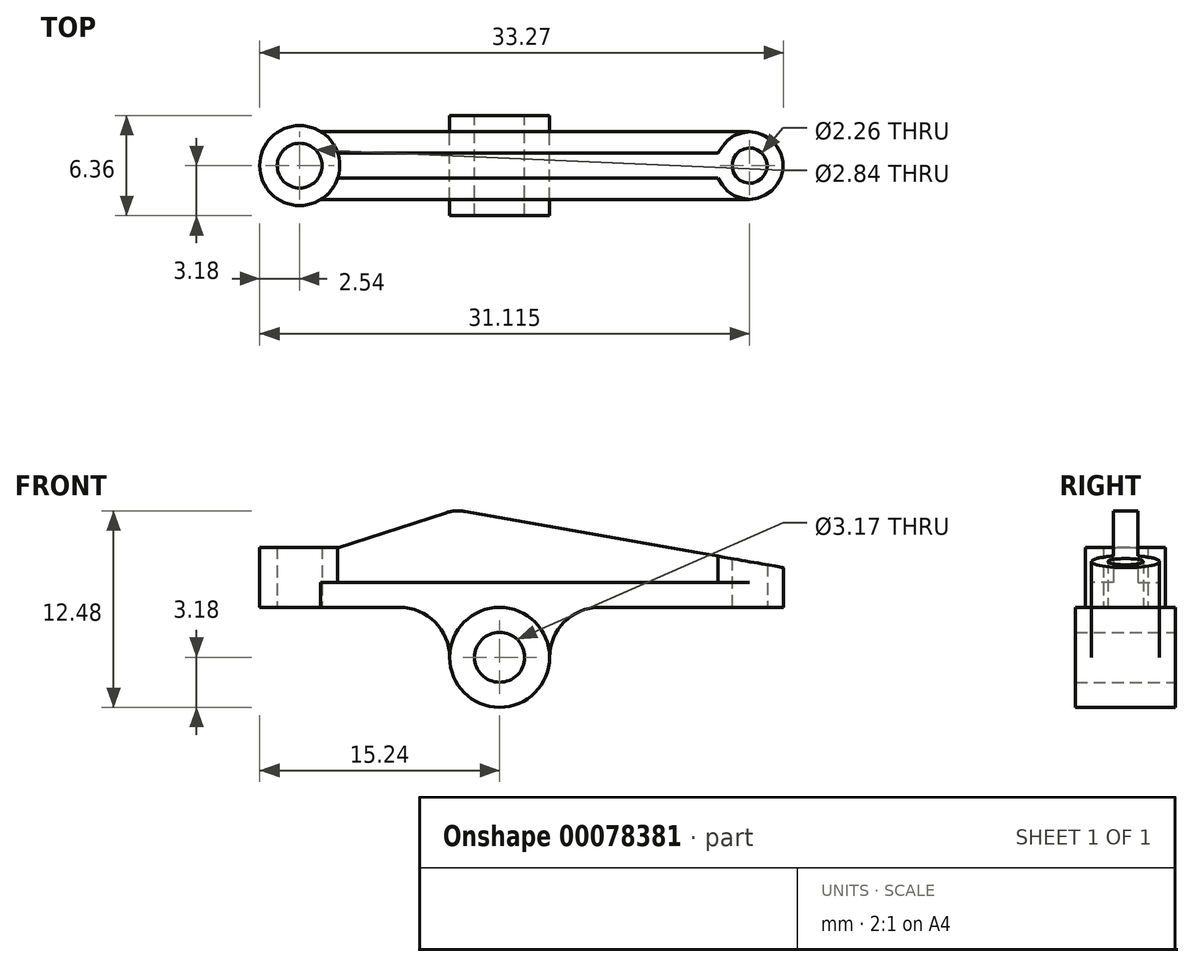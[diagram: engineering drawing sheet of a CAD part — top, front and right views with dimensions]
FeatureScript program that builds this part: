
annotation { "Feature Type Name" : "Feature", "Feature Type Description" : "" }
export const myFeature = defineFeature(function(context is Context, id is Id, definition is map)
    precondition{}
    {
        {
            var Q0;
            Q0=qCreatedBy(makeId("Front.planeOp"),FACE);
            var sketch = newSketch(context, id + "F0", { "sketchPlane" : qUnion([Q0])});
            skCircle(sketch, "E0", {"center": v(0, 0) * mm, "radius": 1.59 * mm});
            skCircle(sketch, "E1", {"center": v(0, 0) * mm, "radius": 3.18 * mm});
            skSolve(sketch);
        }
        {
            var Q0;
            Q0 = qSketchRegion(id + "F0", true);
            extrude(context, id + "F1", {"entities" : qUnion([Q0]), "endBound" : BoundingType.SYMMETRIC, "depth" : 6.35 * mm});
        }
        {
            var Q0;
            Q0=qCreatedBy(makeId("Front.planeOp"),FACE);
            var sketch = newSketch(context, id + "F2", { "sketchPlane" : qUnion([Q0])});
            skLineSegment(sketch, "E2", {"start": v(0, 0) * mm, "end": v(0, 3.18) * mm, "construction": true});
            skSolve(sketch);
        }
        {
            var Q0;
            Q0=qCreatedBy(makeId("Top.planeOp"),FACE);
            cPlane(context, id + "F3", {"entities" : qUnion([Q0]), "cplaneType" : CPlaneType.OFFSET, "offset" : 3.17 * mm, "width" : 152.4 * mm, "height" : 152.4 * mm});
        }
        {
            var Q0;
            Q0=qCreatedBy(id+"F3.planeOp",FACE);
            var sketch = newSketch(context, id + "F4", { "sketchPlane" : qUnion([Q0])});
            skCircle(sketch, "E3", {"center": v(-12.7, 0) * mm, "radius": 1.42 * mm});
            skCircle(sketch, "E4", {"center": v(15.88, 0) * mm, "radius": 1.13 * mm});
            skCircle(sketch, "E5", {"center": v(-12.7, 0) * mm, "radius": 2.54 * mm});
            skCircle(sketch, "E6", {"center": v(15.88, 0) * mm, "radius": 2.16 * mm});
            skSolve(sketch);
        }
        {
            var Q0;
            Q0=qCreatedBy(makeId("Front.planeOp"),FACE);
            var sketch = newSketch(context, id + "F5", { "sketchPlane" : qUnion([Q0])});
            skLineSegment(sketch, "E7", {"start": v(-10.16, 6.99) * mm, "end": v(-3.41, 9.18) * mm});
            skLineSegment(sketch, "E8", {"start": v(-2.19, 9.26) * mm, "end": v(14.01, 6.4) * mm});
            skLineSegment(sketch, "E9", {"start": v(14.01, 6.4) * mm, "end": v(14.01, 3.19) * mm});
            skLineSegment(sketch, "E10", {"start": v(-10.16, 3.18) * mm, "end": v(14.01, 3.19) * mm});
            skPoint(sketch, "E11.visualSharp", {"position": v(-2.81, 9.37) * mm});
            skArc(sketch, "E11.filletArc", {"start": v(-2.19, 9.26) * mm, "mid": v(-2.8, 9.3) * mm, "end": v(-3.41, 9.18) * mm});
            skLineSegment(sketch, "E12", {"start": v(-10.16, 3.18) * mm, "end": v(-11.07, 3.18) * mm});
            skLineSegment(sketch, "E13", {"start": v(-11.07, 3.18) * mm, "end": v(-11.07, 6.69) * mm});
            skLineSegment(sketch, "E14", {"start": v(-10.16, 6.99) * mm, "end": v(-11.07, 6.69) * mm});
            skSolve(sketch);
        }
        {
            var Q0;
            Q0 = qSketchRegion(id + "F5", true);
            extrude(context, id + "F6", {"entities" : qUnion([Q0]), "endBound" : BoundingType.SYMMETRIC, "depth" : 1.57 * mm});
        }
        {
            var Q0;
            Q0=qCreatedBy(makeId("Front.planeOp"),FACE);
            var sketch = newSketch(context, id + "F7", { "sketchPlane" : qUnion([Q0])});
            skLineSegment(sketch, "E15", {"start": v(-2.08, 9.26) * mm, "end": v(18.6, 5.59) * mm});
            skLineSegment(sketch, "E16", {"start": v(18.6, 5.59) * mm, "end": v(18.6, 8.61) * mm});
            skLineSegment(sketch, "E17", {"start": v(18.6, 8.61) * mm, "end": v(-2.08, 9.26) * mm});
            skSolve(sketch);
        }
        {
            var Q0;
            Q0=makeQuery(id+"F4.imprint","IMPRINT",FACE,{"disambiguationData":[TD([[makeQuery(id+"F4.imprint","IMPRINT",EDGE,{"derivedFrom":sQuery(id+"F4.wireOp",EDGE,"E4")}),-1.0]])]});
            extrude(context, id + "F8", {"entities" : qUnion([Q0]), "operationType" : NewBodyOperationType.ADD, "depth" : 3.8 * mm});
        }
        {
            var Q0;
            Q0 = qSketchRegion(id + "F7", true);
            extrude(context, id + "F9", {"entities" : qUnion([Q0]), "operationType" : NewBodyOperationType.REMOVE, "endBound" : BoundingType.SYMMETRIC, "oppositeDirection" : true, "depth" : 25.4 * mm});
        }
        {
            var Q0;
            Q0=qCreatedBy(makeId("Front.planeOp"),FACE);
            var sketch = newSketch(context, id + "F10", { "sketchPlane" : qUnion([Q0])});
            skLineSegment(sketch, "E18", {"start": v(0, 4.75) * mm, "end": v(-12.7, 4.75) * mm});
            skLineSegment(sketch, "E19", {"start": v(-12.7, 4.75) * mm, "end": v(-12.7, 3.18) * mm});
            skLineSegment(sketch, "E20", {"start": v(-12.7, 3.18) * mm, "end": v(-6.35, 3.18) * mm});
            skArc(sketch, "E21.filletArc", {"start": v(-3.18, 0) * mm, "mid": v(-4.1, 2.25) * mm, "end": v(-6.35, 3.18) * mm});
            skArc(sketch, "E22", {"start": v(0, 1.59) * mm, "mid": v(-1.12, 1.12) * mm, "end": v(-1.59, 0) * mm});
            skLineSegment(sketch, "E23", {"start": v(-1.59, 0) * mm, "end": v(-3.18, 0) * mm});
            skPoint(sketch, "E24.start.orphan", {"position": v(0, 3.18) * mm});
            skArc(sketch, "E25.MirrorCS", {"start": v(0, 1.59) * mm, "mid": v(1.12, 1.12) * mm, "end": v(1.59, 0) * mm});
            skLineSegment(sketch, "E26.MirrorCS", {"start": v(1.59, 0) * mm, "end": v(3.18, 0) * mm});
            skArc(sketch, "E27.MirrorCS", {"start": v(3.18, 0) * mm, "mid": v(4.1, 2.25) * mm, "end": v(6.35, 3.18) * mm});
            skLineSegment(sketch, "E28", {"start": v(0, 4.75) * mm, "end": v(15.87, 4.75) * mm});
            skLineSegment(sketch, "E29", {"start": v(15.87, 4.75) * mm, "end": v(15.87, 3.18) * mm});
            skLineSegment(sketch, "E30", {"start": v(15.87, 3.18) * mm, "end": v(6.35, 3.18) * mm});
            skSolve(sketch);
        }
        {
            var Q0;
            Q0 = qSketchRegion(id + "F10", true);
            extrude(context, id + "F11", {"entities" : qUnion([Q0]), "operationType" : NewBodyOperationType.ADD, "endBound" : BoundingType.SYMMETRIC, "depth" : 4.32 * mm});
        }
        {
            var Q0;
            Q0=makeQuery(id+"F11.boolean.opBoolean","SPLIT",FACE,{"disambiguationData":[TD([makeQuery(id+"F8.opExtrude","SWEPT_FACE",FACE,{"disambiguationData":[OSD([sQuery(id+"F4.wireOp",EDGE,"E4")])]})])],"derivedFrom":makeQuery(id+"F11.opExtrude","SWEPT_FACE",FACE,{"disambiguationData":[OSD([sQuery(id+"F10.wireOp",EDGE,"E18"),sQuery(id+"F10.wireOp",EDGE,"E28")])]})});
            var sketch = newSketch(context, id + "F12", { "sketchPlane" : qUnion([Q0])});
            skCircle(sketch, "E31", {"center": v(15.87, 0) * mm, "radius": 1.13 * mm});
            skSolve(sketch);
        }
        {
            var Q0;
            Q0 = qSketchRegion(id + "F12", true);
            extrude(context, id + "F13", {"entities" : qUnion([Q0]), "operationType" : NewBodyOperationType.REMOVE, "oppositeDirection" : true, "depth" : 25.4 * mm});
        }
        {
            var Q0;
            Q0=qCreatedBy(id+"F3.planeOp",FACE);
            var sketch = newSketch(context, id + "F14", { "sketchPlane" : qUnion([Q0])});
            skCircle(sketch, "E32", {"center": v(-12.7, 0) * mm, "radius": 2.54 * mm});
            skCircle(sketch, "E33", {"center": v(-12.7, 0) * mm, "radius": 1.42 * mm});
            skSolve(sketch);
        }
        {
            var Q0;
            Q0=makeQuery(id+"F14.imprint","IMPRINT",FACE,{"disambiguationData":[TD([[makeQuery(id+"F14.imprint","IMPRINT",EDGE,{"derivedFrom":sQuery(id+"F14.wireOp",EDGE,"E32")}),1.0]])]});
            extrude(context, id + "F15", {"entities" : qUnion([Q0]), "operationType" : NewBodyOperationType.ADD, "depth" : 3.8 * mm});
        }
        {
            var Q0;
            {var subQ0=sQuery(id+"F10.wireOp",EDGE,"E19");var subQ1=makeQuery(id+"F11.opExtrude","SWEPT_FACE",FACE,{"disambiguationData":[OSD([subQ0])]});var subQ2=sQuery(id+"F5.wireOp",EDGE,"E13");var subQ5=sQuery(id+"F10.wireOp",EDGE,"E28");var subQ13=sQuery(id+"F10.wireOp",EDGE,"E18");Q0=makeQuery(id+"F15.boolean.opBoolean","SPLIT",FACE,{"disambiguationData":[TD([subQ1])],"derivedFrom":makeQuery(id+"F11.boolean.opBoolean","SPLIT",FACE,{"disambiguationData":[TD([makeQuery(id+"F6.opExtrude","SWEPT_FACE",FACE,{"disambiguationData":[OSD([subQ2])]})])],"derivedFrom":makeQuery(id+"F11.opExtrude","SWEPT_FACE",FACE,{"disambiguationData":[OSD([subQ13,subQ5])]})})});}
            var sketch = newSketch(context, id + "F16", { "sketchPlane" : qUnion([Q0])});
            skCircle(sketch, "E34", {"center": v(-12.7, 0) * mm, "radius": 1.42 * mm});
            skSolve(sketch);
        }
        {
            var Q0;
            Q0 = qSketchRegion(id + "F16", true);
            extrude(context, id + "F17", {"entities" : qUnion([Q0]), "operationType" : NewBodyOperationType.REMOVE, "oppositeDirection" : true, "depth" : 25.4 * mm});
        }
    });
